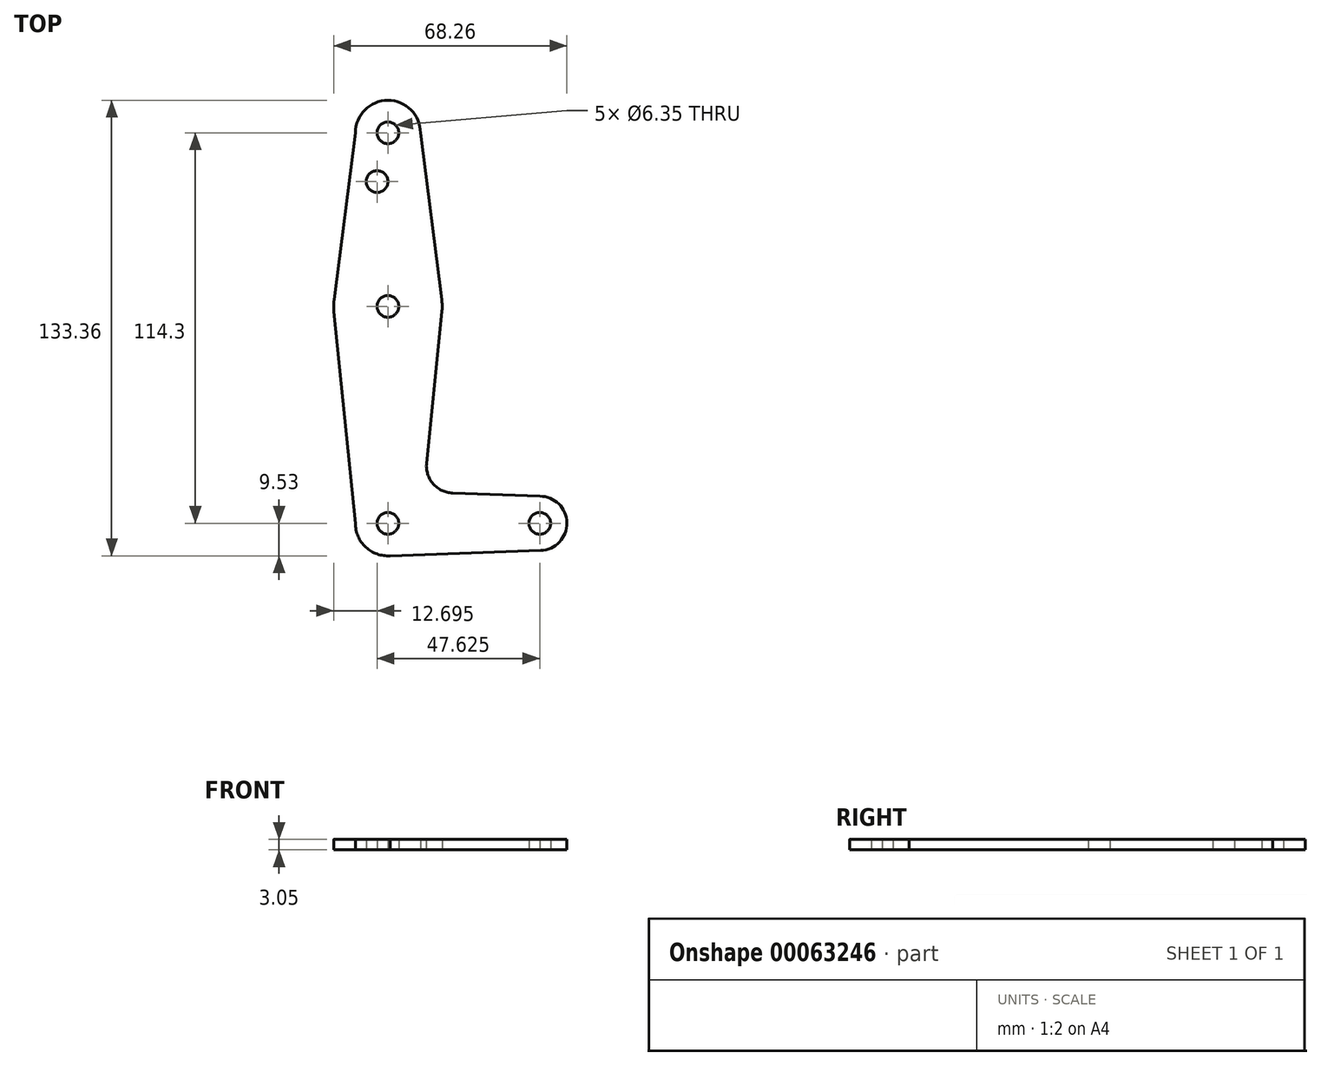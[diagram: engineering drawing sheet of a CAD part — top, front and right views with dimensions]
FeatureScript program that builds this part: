
annotation { "Feature Type Name" : "Feature", "Feature Type Description" : "" }
export const myFeature = defineFeature(function(context is Context, id is Id, definition is map)
    precondition{}
    {
        {
            var Q0;
            Q0=qCreatedBy(makeId("Top.planeOp"),FACE);
            var sketch = newSketch(context, id + "F0", { "sketchPlane" : qUnion([Q0])});
            skLineSegment(sketch, "E0", {"start": v(0, 0) * mm, "end": v(0, 114.3) * mm, "construction": true});
            skLineSegment(sketch, "E1", {"start": v(0, 0) * mm, "end": v(44.45, 0) * mm, "construction": true});
            skCircle(sketch, "E2", {"center": v(0, 0) * mm, "radius": 9.53 * mm});
            skCircle(sketch, "E3", {"center": v(44.45, 0) * mm, "radius": 7.94 * mm});
            skCircle(sketch, "E4", {"center": v(0, 114.3) * mm, "radius": 9.53 * mm});
            skCircle(sketch, "E5", {"center": v(0, 63.5) * mm, "radius": 15.88 * mm});
            skLineSegment(sketch, "E6", {"start": v(0, -9.53) * mm, "end": v(44.73, -7.93) * mm});
            skLineSegment(sketch, "E7", {"start": v(44.45, 7.94) * mm, "end": v(18.93, 8.85) * mm});
            skCircle(sketch, "E8", {"center": v(0, 114.3) * mm, "radius": 3.18 * mm});
            skCircle(sketch, "E9", {"center": v(0, 63.5) * mm, "radius": 3.18 * mm});
            skCircle(sketch, "E10", {"center": v(0, 0) * mm, "radius": 3.18 * mm});
            skCircle(sketch, "E11", {"center": v(44.45, 0) * mm, "radius": 3.18 * mm});
            skCircle(sketch, "E12", {"center": v(-3.18, 100.03) * mm, "radius": 3.18 * mm});
            skLineSegment(sketch, "E13", {"start": v(-9.53, 0) * mm, "end": v(-15.8, 61.9) * mm});
            skLineSegment(sketch, "E14", {"start": v(-9.52, 114.3) * mm, "end": v(-15.75, 65.5) * mm});
            skLineSegment(sketch, "E15", {"start": v(9.52, 114.3) * mm, "end": v(15.75, 65.5) * mm});
            skLineSegment(sketch, "E16", {"start": v(11.3, 17.6) * mm, "end": v(15.8, 61.9) * mm});
            skArc(sketch, "E17.filletArc", {"start": v(11.3, 17.6) * mm, "mid": v(13.22, 11.57) * mm, "end": v(18.93, 8.85) * mm});
            skSolve(sketch);
        }
        {
            var Q0;
            Q0 = qSketchRegion(id + "F0", true);
            extrude(context, id + "F1", {"entities" : qUnion([Q0]), "depth" : 3.05 * mm});
        }
    });
